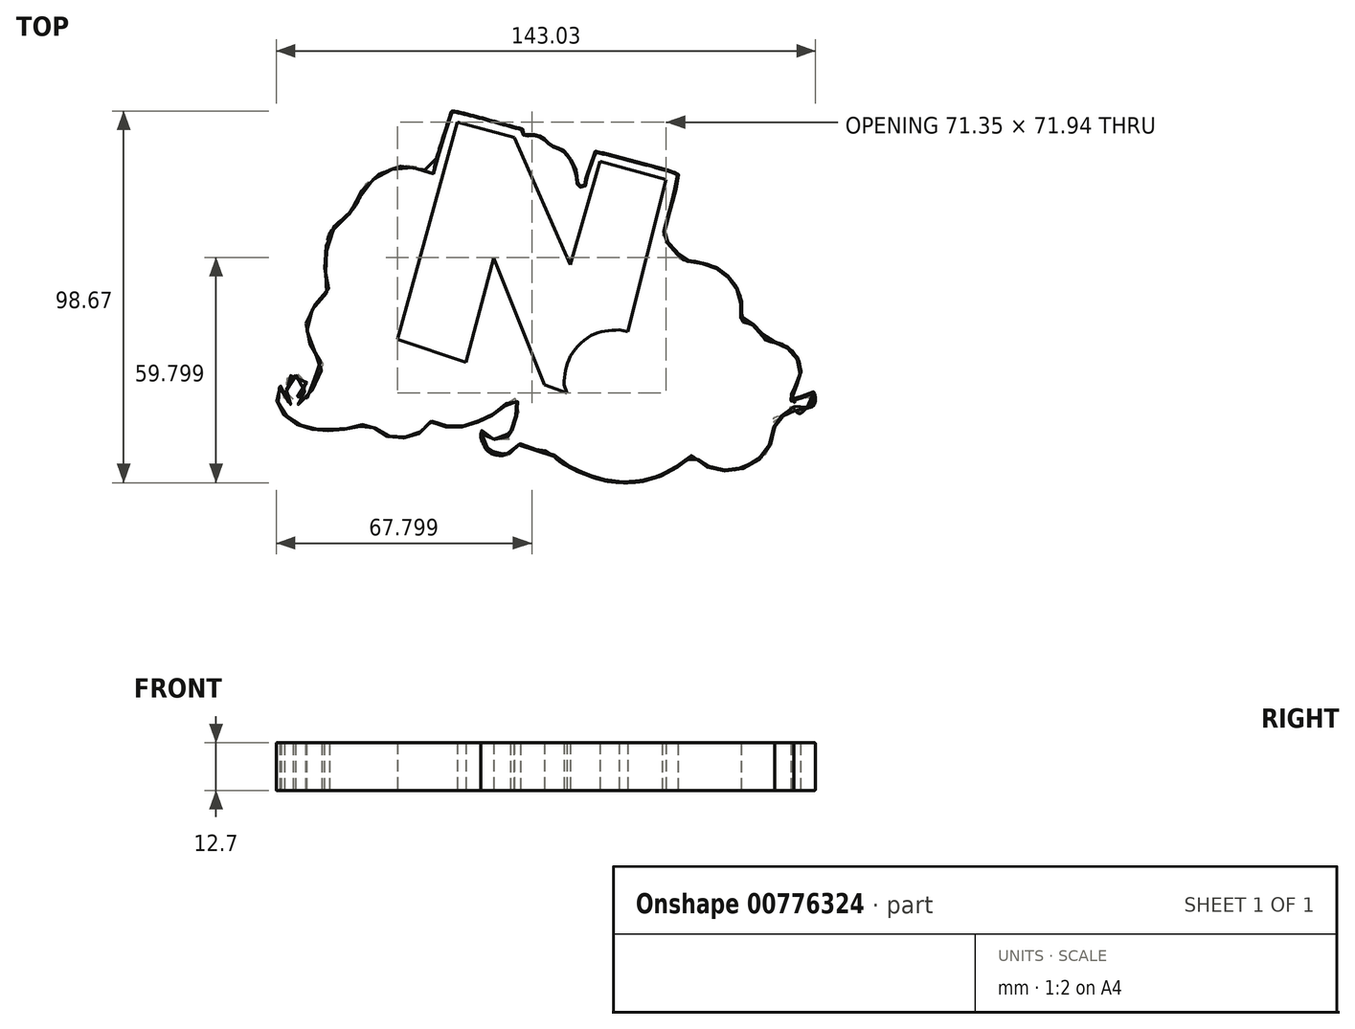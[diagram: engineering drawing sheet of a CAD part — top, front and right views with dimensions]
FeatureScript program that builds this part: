
annotation { "Feature Type Name" : "Feature", "Feature Type Description" : "" }
export const myFeature = defineFeature(function(context is Context, id is Id, definition is map)
    precondition{}
    {
        {
            var Q0;
            Q0=qCreatedBy(makeId("Top.planeOp"),FACE);
            var sketch = newSketch(context, id + "F0", { "sketchPlane" : qUnion([Q0])});
            skFitSpline(sketch, "E0", {"points": [v(-59.76, 5.34) * mm, v(-63.34, 11.66) * mm, v(-62.32, 19.85) * mm, v(-57.54, 26) * mm, v(-58.56, 28.22) * mm, v(-58.73, 33.86) * mm, v(-57.03, 40.69) * mm, v(-50.88, 47) * mm, v(-49.17, 51.1) * mm, v(-46.54, 54.1) * mm, v(-41.83, 56.87) * mm, v(-34.89, 57.48) * mm, v(-30.06, 55.97) * mm, v(-29.88, 56.93) * mm, v(-25.4, 71.9) * mm, v(-25.34, 72.17) * mm, v(-24.86, 72.32) * mm, v(-6.58, 67.66) * mm, v(-6.46, 67.63) * mm, v(-5.92, 66) * mm, v(-5.58, 65.9) * mm, v(-2.78, 66) * mm, v(-0.4, 64.8) * mm, v(1.42, 63.2) * mm, v(4.08, 62.1) * mm, v(7.79, 56.34) * mm, v(8.33, 52.54) * mm, v(8.6, 52.42) * mm, v(9.84, 52.3) * mm, v(10.08, 53.11) * mm, v(12.83, 61.56) * mm, v(13.2, 61.65) * mm, v(34.63, 55.74) * mm, v(34.9, 55.37) * mm, v(34.87, 54.44) * mm, v(30.84, 38.68) * mm, v(30.9, 38.4) * mm, v(34.2, 35.47) * mm, v(35.58, 33) * mm, v(35.88, 32.86) * mm, v(44, 31.22) * mm, v(49.35, 27.13) * mm, v(51.61, 22.03) * mm, v(51.76, 16.93) * mm, v(52.11, 16.61) * mm, v(55.6, 15.21) * mm, v(57.97, 11.84) * mm, v(58.82, 11.48) * mm, v(63.83, 9.76) * mm, v(67.52, 3.3) * mm, v(65.23, -2.9) * mm, v(65.18, -4.78) * mm, v(65.79, -4.88) * mm, v(66.55, -3.66) * mm, v(68.1, -3.54) * mm, v(68.89, -3.92) * mm, v(69.98, -3.44) * mm, v(70.54, -2.37) * mm, v(70.84, -2.22) * mm, v(71.17, -3.23) * mm, v(71.22, -4.76) * mm, v(70.74, -5.92) * mm, v(69.78, -6.38) * mm, v(68.53, -6.84) * mm, v(67.24, -7.95) * mm, v(65.56, -6.76) * mm, v(65.51, -6.23) * mm, v(65.3, -6.23) * mm, v(64.9, -6.3) * mm, v(64.44, -7.47) * mm, v(63.05, -8.51) * mm, v(61.68, -9.05) * mm, v(60.4, -9.12) * mm, v(60.35, -9.79) * mm, v(60.32, -12.78) * mm, v(59.56, -15.55) * mm, v(58.6, -17.99) * mm, v(56.67, -19.94) * mm, v(54.2, -21.49) * mm, v(50.96, -22.9) * mm, v(47.25, -23.14) * mm, v(46.82, -23.14) * mm, v(42.12, -21.95) * mm, v(39.18, -19.56) * mm, v(38.85, -19.25) * mm, v(38.54, -19.28) * mm, v(38.26, -19.64) * mm, v(30.51, -24.44) * mm, v(23.37, -26.2) * mm, v(14.4, -25.55) * mm, v(2.65, -20.1) * mm, v(0.93, -18.4) * mm, v(-3.99, -17.55) * mm, v(-6.9, -16.24) * mm, v(-8.71, -17.52) * mm, v(-9.89, -18.8) * mm, v(-11.94, -19.1) * mm, v(-14.71, -18.63) * mm, v(-16.48, -16.84) * mm, v(-17.47, -14.13) * mm, v(-17.4, -12.93) * mm, v(-17.23, -12.46) * mm, v(-16.93, -13.44) * mm, v(-15.76, -14.79) * mm, v(-14.11, -14.77) * mm, v(-12.3, -13.25) * mm, v(-11.72, -13.1) * mm, v(-10.6, -13.31) * mm, v(-9.44, -14.64) * mm, v(-8.71, -14.15) * mm, v(-8.9, -13.74) * mm, v(-9.6, -11.72) * mm, v(-9, -9.6) * mm, v(-8.67, -9.2) * mm, v(-7.02, -6.42) * mm, v(-7.15, -6) * mm, v(-8.76, -3.9) * mm, v(-9.23, -4.02) * mm, v(-12.08, -6.9) * mm, v(-17.84, -10.1) * mm, v(-22.69, -11.54) * mm, v(-29.8, -10.83) * mm, v(-30.7, -10.17) * mm, v(-31.2, -10.47) * mm, v(-32.92, -12.63) * mm, v(-36.83, -14.3) * mm, v(-40.7, -14.4) * mm, v(-44.82, -12.73) * mm, v(-46.83, -10.62) * mm, v(-47.41, -10.6) * mm, v(-49.8, -11.49) * mm, v(-58.96, -12.48) * mm, v(-65.61, -11.16) * mm, v(-70.59, -7.4) * mm, v(-71.7, -4.1) * mm, v(-71.35, -1.2) * mm, v(-70.54, -0.7) * mm, v(-70.64, -1) * mm, v(-70.6, -2.65) * mm, v(-69.32, -4.3) * mm, v(-67.5, -5.3) * mm, v(-67.17, -3.79) * mm, v(-67.38, -3.54) * mm, v(-68.57, -3.07) * mm, v(-69.32, -1.88) * mm, v(-69.47, 0) * mm, v(-69.04, 1.13) * mm, v(-67.28, 2.39) * mm, v(-65.09, 1.89) * mm, v(-63.76, 0.38) * mm, v(-63.58, 0) * mm, v(-64.05, -2.03) * mm, v(-65.34, -3.36) * mm, v(-66.38, -3.72) * mm, v(-66.23, -5.33) * mm, v(-63.69, -3.86) * mm, v(-63.22, -3.5) * mm, v(-62.36, -1.49) * mm, v(-61.39, 1.85) * mm, v(-59.56, 4.4) * mm, v(-59.76, 5.34) * mm]});
            skSolve(sketch);
        }
        {
            var Q0;
            Q0 = qSketchRegion(id + "F0", true);
            extrude(context, id + "F1", {"entities" : qUnion([Q0]), "depth" : 12.7 * mm, "offsetDistance" : 25.4 * mm});
        }
        {
            var Q0;
            Q0=qCreatedBy(makeId("Top.planeOp"),FACE);
            var sketch = newSketch(context, id + "F2", { "sketchPlane" : qUnion([Q0])});
            skLineSegment(sketch, "E1", {"start": v(-22.76, 7.81) * mm, "end": v(-38.05, 12.55) * mm});
            skLineSegment(sketch, "E2", {"start": v(-38.05, 12.55) * mm, "end": v(-22.86, 67.84) * mm});
            skLineSegment(sketch, "E3", {"start": v(-22.86, 67.84) * mm, "end": v(-9.5, 64.17) * mm});
            skLineSegment(sketch, "E4", {"start": v(-9.5, 64.17) * mm, "end": v(6.45, 25.32) * mm});
            skLineSegment(sketch, "E5", {"start": v(6.45, 25.32) * mm, "end": v(15.6, 57.08) * mm});
            skLineSegment(sketch, "E6", {"start": v(15.6, 57.08) * mm, "end": v(29.49, 52.92) * mm});
            skLineSegment(sketch, "E7", {"start": v(29.49, 52.92) * mm, "end": v(19.2, 14.2) * mm});
            skLineSegment(sketch, "E8", {"start": v(-22.76, 7.81) * mm, "end": v(-14.53, 39.12) * mm});
            skLineSegment(sketch, "E9", {"start": v(-14.53, 39.12) * mm, "end": v(1.09, 1.07) * mm});
            skLineSegment(sketch, "E10", {"start": v(1.09, 1.07) * mm, "end": v(4.59, -0.33) * mm});
            skFitSpline(sketch, "E11", {"points": [v(4.59, -0.33) * mm, v(6, 6.7) * mm, v(12.35, 13.01) * mm, v(19.2, 14.2) * mm], "startDerivative": vector(1.26, 22.01) * mm, "endDerivative": vector(21.72, 0.59) * mm});
            skLineSegment(sketch, "E12", {"start": v(4.59, -0.33) * mm, "end": v(5.34, -2.5) * mm});
            skLineSegment(sketch, "E13", {"start": v(5.34, -2.5) * mm, "end": v(-0.64, -0.33) * mm});
            skLineSegment(sketch, "E14", {"start": v(-0.64, -0.33) * mm, "end": v(-14.07, 33.37) * mm});
            skLineSegment(sketch, "E15", {"start": v(-14.07, 33.37) * mm, "end": v(-21.5, 5.62) * mm});
            skLineSegment(sketch, "E16", {"start": v(-21.5, 5.62) * mm, "end": v(-39.65, 11.68) * mm});
            skLineSegment(sketch, "E17", {"start": v(-39.65, 11.68) * mm, "end": v(-23.77, 69.43) * mm});
            skLineSegment(sketch, "E18", {"start": v(-23.77, 69.43) * mm, "end": v(-8.63, 65.27) * mm});
            skLineSegment(sketch, "E19", {"start": v(-8.63, 65.27) * mm, "end": v(6.25, 31.54) * mm});
            skLineSegment(sketch, "E20", {"start": v(6.25, 31.54) * mm, "end": v(14.14, 58.93) * mm});
            skLineSegment(sketch, "E21", {"start": v(14.14, 58.93) * mm, "end": v(31.7, 54.1) * mm});
            skLineSegment(sketch, "E22", {"start": v(31.7, 54.1) * mm, "end": v(21.45, 13.78) * mm});
            skLineSegment(sketch, "E23", {"start": v(21.45, 13.78) * mm, "end": v(19.2, 14.2) * mm});
            skSolve(sketch);
        }
        {
            var Q0;
            Q0 = qSketchRegion(id + "F2", true);
            extrude(context, id + "F3", {"entities" : qUnion([Q0]), "operationType" : NewBodyOperationType.REMOVE, "depth" : 25.4 * mm, "offsetDistance" : 25.4 * mm});
        }
        {
            var Q0;
            Q0=makeQuery(id+"F1.opExtrude","CAP_EDGE",EDGE,{"disambiguationData":[OSD([sQuery(id+"F0.wireOp",EDGE,"E0")])],"isStart":false});
            var Q1;
            Q1=makeQuery(id+"F1.opExtrude","CAP_EDGE",EDGE,{"disambiguationData":[OSD([sQuery(id+"F0.wireOp",EDGE,"E0")])],"isStart":true});
            fillet(context, id + "F4", {"entities" : qUnion([Q0, Q1]), "radius" : 0.25 * mm, "tangentPropagation" : true, "allowEdgeOverflow" : false});
        }
    });
